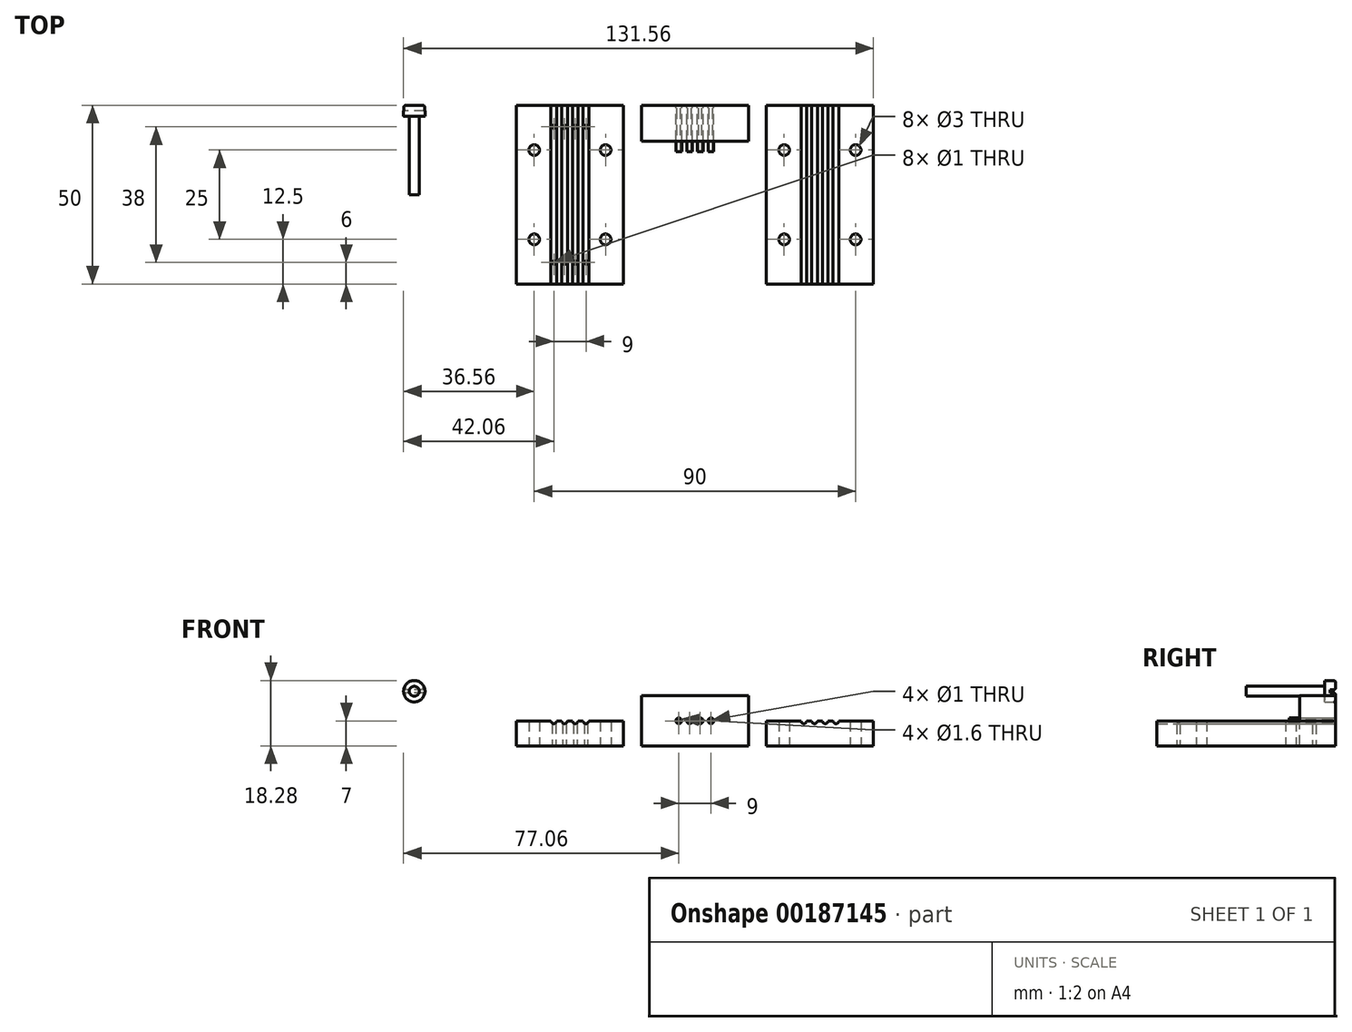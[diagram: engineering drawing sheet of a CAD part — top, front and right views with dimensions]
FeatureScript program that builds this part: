
annotation { "Feature Type Name" : "Feature", "Feature Type Description" : "" }
export const myFeature = defineFeature(function(context is Context, id is Id, definition is map)
    precondition{}
    {
        {
            var Q0;
            Q0=qCreatedBy(makeId("Front.planeOp"),FACE);
            var sketch = newSketch(context, id + "F0", { "sketchPlane" : qUnion([Q0])});
            skLineSegment(sketch, "E0.bottom", {"start": v(0, 0) * mm, "end": v(30, 0) * mm});
            skLineSegment(sketch, "E0.top", {"start": v(0, 7) * mm, "end": v(30, 7) * mm});
            skLineSegment(sketch, "E0.left", {"start": v(0, 0) * mm, "end": v(0, 7) * mm});
            skLineSegment(sketch, "E0.right", {"start": v(30, 0) * mm, "end": v(30, 7) * mm});
            skCircle(sketch, "E1", {"center": v(10.5, 7) * mm, "radius": 0.8 * mm});
            skCircle(sketch, "E2.1.0.0", {"center": v(13.5, 7) * mm, "radius": 0.8 * mm});
            skCircle(sketch, "E2.2.0.0", {"center": v(16.5, 7) * mm, "radius": 0.8 * mm});
            skCircle(sketch, "E2.3.0.0", {"center": v(19.5, 7) * mm, "radius": 0.8 * mm});
            skLineSegment(sketch, "E2.direction1", {"start": v(10.5, 7) * mm, "end": v(13.5, 7) * mm, "construction": true});
            skSolve(sketch);
        }
        {
            var Q0;
            Q0=makeQuery(id+"F0.imprint","IMPRINT",FACE,{"disambiguationData":[TD([[makeQuery(id+"F0.imprint","IMPRINT",EDGE,{"derivedFrom":sQuery(id+"F0.wireOp",EDGE,"E0.bottom")}),1.0]])]});
            extrude(context, id + "F1", {"entities" : qUnion([Q0]), "depth" : 50 * mm});
        }
        {
            var Q0;
            Q0=qCreatedBy(makeId("Front.planeOp"),FACE);
            var sketch = newSketch(context, id + "F2", { "sketchPlane" : qUnion([Q0])});
            skLineSegment(sketch, "E3.bottom", {"start": v(35, 0) * mm, "end": v(65, 0) * mm});
            skLineSegment(sketch, "E3.top", {"start": v(35, 7) * mm, "end": v(65, 7) * mm, "construction": true});
            skLineSegment(sketch, "E3.left", {"start": v(35, 0) * mm, "end": v(35, 7) * mm});
            skLineSegment(sketch, "E3.right", {"start": v(65, 0) * mm, "end": v(65, 7) * mm});
            skCircle(sketch, "E4", {"center": v(45.5, 7) * mm, "radius": 0.8 * mm});
            skCircle(sketch, "E5.1.0.0", {"center": v(48.5, 7) * mm, "radius": 0.8 * mm});
            skCircle(sketch, "E5.2.0.0", {"center": v(51.5, 7) * mm, "radius": 0.8 * mm});
            skCircle(sketch, "E5.3.0.0", {"center": v(54.5, 7) * mm, "radius": 0.8 * mm});
            skLineSegment(sketch, "E5.direction1", {"start": v(45.5, 7) * mm, "end": v(48.5, 7) * mm, "construction": true});
            skLineSegment(sketch, "E6.top", {"start": v(35, 14) * mm, "end": v(65, 14) * mm});
            skLineSegment(sketch, "E6.left", {"start": v(35, 0) * mm, "end": v(35, 14) * mm});
            skLineSegment(sketch, "E6.right", {"start": v(65, 0) * mm, "end": v(65, 14) * mm});
            skCircle(sketch, "E7", {"center": v(45.5, 7) * mm, "radius": 0.5 * mm});
            skCircle(sketch, "E8.1.0.0", {"center": v(48.5, 7) * mm, "radius": 0.5 * mm});
            skCircle(sketch, "E8.2.0.0", {"center": v(51.5, 7) * mm, "radius": 0.5 * mm});
            skCircle(sketch, "E8.3.0.0", {"center": v(54.5, 7) * mm, "radius": 0.5 * mm});
            skSolve(sketch);
        }
        {
            var Q0;
            Q0=makeQuery(id+"F2.imprint","IMPRINT",FACE,{"disambiguationData":[TD([[makeQuery(id+"F2.imprint","IMPRINT",EDGE,{"derivedFrom":sQuery(id+"F2.wireOp",EDGE,"E5.3.0.0")}),1.0]])]});
            var Q1;
            Q1=makeQuery(id+"F2.imprint","IMPRINT",FACE,{"disambiguationData":[TD([[makeQuery(id+"F2.imprint","IMPRINT",EDGE,{"derivedFrom":sQuery(id+"F2.wireOp",EDGE,"E5.2.0.0")}),1.0]])]});
            var Q2;
            Q2=makeQuery(id+"F2.imprint","IMPRINT",FACE,{"disambiguationData":[TD([[makeQuery(id+"F2.imprint","IMPRINT",EDGE,{"derivedFrom":sQuery(id+"F2.wireOp",EDGE,"E5.1.0.0")}),1.0]])]});
            var Q3;
            Q3=makeQuery(id+"F2.imprint","IMPRINT",FACE,{"disambiguationData":[TD([[makeQuery(id+"F2.imprint","IMPRINT",EDGE,{"derivedFrom":sQuery(id+"F2.wireOp",EDGE,"E4")}),1.0]])]});
            extrude(context, id + "F3", {"entities" : qUnion([Q0, Q1, Q2, Q3]), "depth" : 13 * mm});
        }
        {
            var Q0;
            Q0=makeQuery(id+"F2.imprint","IMPRINT",FACE,{"disambiguationData":[TD([[makeQuery(id+"F2.imprint","IMPRINT",EDGE,{"derivedFrom":sQuery(id+"F2.wireOp",EDGE,"E4")}),-1.0]])]});
            extrude(context, id + "F4", {"entities" : qUnion([Q0]), "depth" : 10 * mm});
        }
        {
            var Q0;
            Q0=qCreatedBy(makeId("Front.planeOp"),FACE);
            var sketch = newSketch(context, id + "F5", { "sketchPlane" : qUnion([Q0])});
            skCircle(sketch, "E9", {"center": v(-28.56, 15.28) * mm, "radius": 3 * mm});
            skCircle(sketch, "E10", {"center": v(-28.56, 15.28) * mm, "radius": 1.4 * mm});
            skSolve(sketch);
        }
        {
            var Q0;
            Q0=makeQuery(id+"F5.imprint","IMPRINT",FACE,{"disambiguationData":[TD([[makeQuery(id+"F5.imprint","IMPRINT",EDGE,{"derivedFrom":sQuery(id+"F5.wireOp",EDGE,"E9")}),1.0]])]});
            var Q1;
            Q1=makeQuery(id+"F5.imprint","IMPRINT",FACE,{"disambiguationData":[TD([[makeQuery(id+"F5.imprint","IMPRINT",EDGE,{"derivedFrom":sQuery(id+"F5.wireOp",EDGE,"E10")}),1.0]])]});
            extrude(context, id + "F6", {"entities" : qUnion([Q0, Q1]), "depth" : 3 * mm});
        }
        {
            var Q0;
            Q0=makeQuery(id+"F5.imprint","IMPRINT",FACE,{"disambiguationData":[TD([[makeQuery(id+"F5.imprint","IMPRINT",EDGE,{"derivedFrom":sQuery(id+"F5.wireOp",EDGE,"E10")}),1.0]])]});
            extrude(context, id + "F7", {"entities" : qUnion([Q0]), "operationType" : NewBodyOperationType.ADD, "depth" : 25 * mm});
        }
        {
            var Q0;
            Q0=makeQuery(id+"F5.imprint","IMPRINT",FACE,{"disambiguationData":[TD([[makeQuery(id+"F5.imprint","IMPRINT",EDGE,{"derivedFrom":sQuery(id+"F5.wireOp",EDGE,"E9")}),1.0]])]});
            var sketch = newSketch(context, id + "F8", { "sketchPlane" : qUnion([Q0])});
            skCircle(sketch, "E11.0", {"center": v(-28.56, 15.28) * mm, "radius": 1.4 * mm});
            skLineSegment(sketch, "E12.bottom", {"start": v(-24.57, 14.84) * mm, "end": v(-32.56, 14.84) * mm});
            skLineSegment(sketch, "E12.top", {"start": v(-24.57, 15.72) * mm, "end": v(-32.56, 15.72) * mm});
            skLineSegment(sketch, "E12.left", {"start": v(-24.57, 14.84) * mm, "end": v(-24.57, 15.72) * mm});
            skLineSegment(sketch, "E12.right", {"start": v(-32.56, 14.84) * mm, "end": v(-32.56, 15.72) * mm});
            skSolve(sketch);
        }
        {
            var Q0;
            {var subQ0=sQuery(id+"F8.wireOp",EDGE,"E12.top");var subQ1=sQuery(id+"F8.wireOp",EDGE,"E11.0");var subQ2=makeQuery(id+"F8.imprint","INTERSECT",VERTEX,{"disambiguationData":[OD(0.0)],"derivedFrom":[subQ1,subQ0]});Q0=makeQuery(id+"F8.imprint","IMPRINT",FACE,{"disambiguationData":[TD([[makeQuery(id+"F8.imprint","IMPRINT",EDGE,{"disambiguationData":[TD([[subQ2,-1.0]])],"derivedFrom":subQ1}),-1.0]])]});}
            var Q1;
            {var subQ0=sQuery(id+"F8.wireOp",EDGE,"E12.top");var subQ1=sQuery(id+"F8.wireOp",EDGE,"E11.0");var subQ2=makeQuery(id+"F8.imprint","INTERSECT",VERTEX,{"disambiguationData":[OD(0.0)],"derivedFrom":[subQ1,subQ0]});Q1=makeQuery(id+"F8.imprint","IMPRINT",FACE,{"disambiguationData":[TD([[makeQuery(id+"F8.imprint","IMPRINT",EDGE,{"disambiguationData":[TD([[subQ2,-1.0]])],"derivedFrom":subQ1}),1.0]])]});}
            var Q2;
            {var subQ0=sQuery(id+"F8.wireOp",EDGE,"E12.top");var subQ1=sQuery(id+"F8.wireOp",EDGE,"E11.0");var subQ2=makeQuery(id+"F8.imprint","INTERSECT",VERTEX,{"disambiguationData":[OD(1.0)],"derivedFrom":[subQ1,subQ0]});Q2=makeQuery(id+"F8.imprint","IMPRINT",FACE,{"disambiguationData":[TD([[makeQuery(id+"F8.imprint","IMPRINT",EDGE,{"disambiguationData":[TD([[subQ2,1.0]])],"derivedFrom":subQ1}),-1.0]])]});}
            extrude(context, id + "F9", {"entities" : qUnion([Q0, Q1, Q2]), "operationType" : NewBodyOperationType.REMOVE, "depth" : 1.5 * mm});
        }
        {
            var Q0;
            {var subQ0=sQuery(id+"F5.wireOp",EDGE,"E9");Q0=makeQuery(id+"F9.boolean.opBoolean","SPLIT",FACE,{"disambiguationData":[TD([makeQuery(id+"F9.opExtrude","SWEPT_FACE",FACE,{"disambiguationData":[OSD([sQuery(id+"F8.wireOp",EDGE,"E12.top")])]})])],"derivedFrom":makeQuery(id+"F6.opExtrude","CAP_FACE",FACE,{"disambiguationData":[OSD([subQ0])],"isStart":true})});}
            var Q1;
            {var subQ0=sQuery(id+"F5.wireOp",EDGE,"E9");Q1=makeQuery(id+"F9.boolean.opBoolean","SPLIT",FACE,{"disambiguationData":[TD([makeQuery(id+"F9.opExtrude","SWEPT_FACE",FACE,{"disambiguationData":[OSD([sQuery(id+"F8.wireOp",EDGE,"E12.bottom")])]})])],"derivedFrom":makeQuery(id+"F6.opExtrude","CAP_FACE",FACE,{"disambiguationData":[OSD([subQ0])],"isStart":true})});}
            fillet(context, id + "F10", {"entities" : qUnion([Q0, Q1]), "radius" : .5 * mm, "tangentPropagation" : true, "allowEdgeOverflow" : false});
        }
        {
            var Q0;
            Q0=makeQuery(id+"F1.opExtrude","SWEPT_FACE",FACE,{"disambiguationData":[OSD([sQuery(id+"F0.wireOp",EDGE,"E0.bottom")])]});
            var sketch = newSketch(context, id + "F11", { "sketchPlane" : qUnion([Q0])});
            skLineSegment(sketch, "E13", {"start": v(30, 50) * mm, "end": v(0, 0) * mm, "construction": true});
            skLineSegment(sketch, "E14.bottom", {"start": v(25, 37.5) * mm, "end": v(5, 37.5) * mm, "construction": true});
            skLineSegment(sketch, "E14.top", {"start": v(25, 12.5) * mm, "end": v(5, 12.5) * mm, "construction": true});
            skLineSegment(sketch, "E14.left", {"start": v(25, 37.5) * mm, "end": v(25, 12.5) * mm, "construction": true});
            skLineSegment(sketch, "E14.right", {"start": v(5, 37.5) * mm, "end": v(5, 12.5) * mm, "construction": true});
            skPoint(sketch, "E14.middle", {"position": v(15, 25) * mm});
            skCircle(sketch, "E15", {"center": v(5, 12.5) * mm, "radius": 1.5 * mm});
            skCircle(sketch, "E16.0.1.0", {"center": v(5, 37.5) * mm, "radius": 1.5 * mm});
            skCircle(sketch, "E16.1.0.0", {"center": v(25, 12.5) * mm, "radius": 1.5 * mm});
            skCircle(sketch, "E16.1.1.0", {"center": v(25, 37.5) * mm, "radius": 1.5 * mm});
            skLineSegment(sketch, "E16.direction1", {"start": v(5, 12.5) * mm, "end": v(25, 12.5) * mm, "construction": true});
            skLineSegment(sketch, "E16.direction2", {"start": v(5, 12.5) * mm, "end": v(5, 37.5) * mm, "construction": true});
            skLineSegment(sketch, "E17.bottom", {"start": v(19.5, 44) * mm, "end": v(10.5, 44) * mm, "construction": true});
            skLineSegment(sketch, "E17.top", {"start": v(19.5, 6) * mm, "end": v(10.5, 6) * mm, "construction": true});
            skLineSegment(sketch, "E17.left", {"start": v(19.5, 44) * mm, "end": v(19.5, 6) * mm, "construction": true});
            skLineSegment(sketch, "E17.right", {"start": v(10.5, 44) * mm, "end": v(10.5, 6) * mm, "construction": true});
            skCircle(sketch, "E18", {"center": v(10.5, 6) * mm, "radius": 0.5 * mm});
            skCircle(sketch, "E19.0.1.0", {"center": v(10.5, 44) * mm, "radius": 0.5 * mm});
            skCircle(sketch, "E19.1.0.0", {"center": v(13.5, 6) * mm, "radius": 0.5 * mm});
            skCircle(sketch, "E19.1.1.0", {"center": v(13.5, 44) * mm, "radius": 0.5 * mm});
            skCircle(sketch, "E19.2.0.0", {"center": v(16.5, 6) * mm, "radius": 0.5 * mm});
            skCircle(sketch, "E19.2.1.0", {"center": v(16.5, 44) * mm, "radius": 0.5 * mm});
            skCircle(sketch, "E19.3.0.0", {"center": v(19.5, 6) * mm, "radius": 0.5 * mm});
            skCircle(sketch, "E19.3.1.0", {"center": v(19.5, 44) * mm, "radius": 0.5 * mm});
            skLineSegment(sketch, "E19.direction1", {"start": v(10.5, 6) * mm, "end": v(13.5, 6) * mm, "construction": true});
            skLineSegment(sketch, "E19.direction2", {"start": v(10.5, 6) * mm, "end": v(10.5, 44) * mm, "construction": true});
            skSolve(sketch);
        }
        {
            var Q0;
            Q0=makeQuery(id+"F1.opExtrude","SWEPT_BODY",BODY,{"disambiguationData":[OSD([sQuery(id+"F0.wireOp",EDGE,"E0.bottom"),sQuery(id+"F0.wireOp",EDGE,"E0.top"),sQuery(id+"F0.wireOp",EDGE,"E0.left"),sQuery(id+"F0.wireOp",EDGE,"E0.right"),sQuery(id+"F0.wireOp",EDGE,"E1"),sQuery(id+"F0.wireOp",EDGE,"E2.1.0.0"),sQuery(id+"F0.wireOp",EDGE,"E2.2.0.0"),sQuery(id+"F0.wireOp",EDGE,"E2.3.0.0")])]});
            transform(context, id + "F12", {"entities" : qUnion([Q0]), "transformType" : TransformType.TRANSLATION_3D, "dx" : 70 * mm, "dy" : 0 * mm, "dz" : 0 * mm, "makeCopy" : true});
        }
        {
            var Q0;
            Q0 = qSketchRegion(id + "F11", true);
            extrude(context, id + "F13", {"entities" : qUnion([Q0]), "operationType" : NewBodyOperationType.REMOVE, "oppositeDirection" : true, "depth" : 25 * mm});
        }
        {
            var Q0;
            Q0=makeQuery(id+"F12.opPattern","COPY",FACE,{"derivedFrom":makeQuery(id+"F1.opExtrude","SWEPT_FACE",FACE,{"disambiguationData":[OSD([sQuery(id+"F0.wireOp",EDGE,"E0.bottom")])]}),"instanceName":"1"});
            var sketch = newSketch(context, id + "F14", { "sketchPlane" : qUnion([Q0])});
            skLineSegment(sketch, "E20", {"start": v(70, 0) * mm, "end": v(100, 50) * mm, "construction": true});
            skLineSegment(sketch, "E21.bottom", {"start": v(75, 12.5) * mm, "end": v(95, 12.5) * mm, "construction": true});
            skLineSegment(sketch, "E21.top", {"start": v(75, 37.5) * mm, "end": v(95, 37.5) * mm, "construction": true});
            skLineSegment(sketch, "E21.left", {"start": v(75, 12.5) * mm, "end": v(75, 37.5) * mm, "construction": true});
            skLineSegment(sketch, "E21.right", {"start": v(95, 12.5) * mm, "end": v(95, 37.5) * mm, "construction": true});
            skPoint(sketch, "E21.middle", {"position": v(85, 25) * mm});
            skCircle(sketch, "E22", {"center": v(95, 37.5) * mm, "radius": 1.5 * mm});
            skCircle(sketch, "E23.0.1.0", {"center": v(95, 12.5) * mm, "radius": 1.5 * mm});
            skCircle(sketch, "E23.1.0.0", {"center": v(75, 37.5) * mm, "radius": 1.5 * mm});
            skCircle(sketch, "E23.1.1.0", {"center": v(75, 12.5) * mm, "radius": 1.5 * mm});
            skLineSegment(sketch, "E23.direction1", {"start": v(95, 37.5) * mm, "end": v(75, 37.5) * mm, "construction": true});
            skLineSegment(sketch, "E23.direction2", {"start": v(95, 37.5) * mm, "end": v(95, 12.5) * mm, "construction": true});
            skSolve(sketch);
        }
        {
            var Q0;
            Q0 = qSketchRegion(id + "F14", true);
            extrude(context, id + "F15", {"entities" : qUnion([Q0]), "operationType" : NewBodyOperationType.REMOVE, "oppositeDirection" : true, "depth" : 25 * mm});
        }
    });
